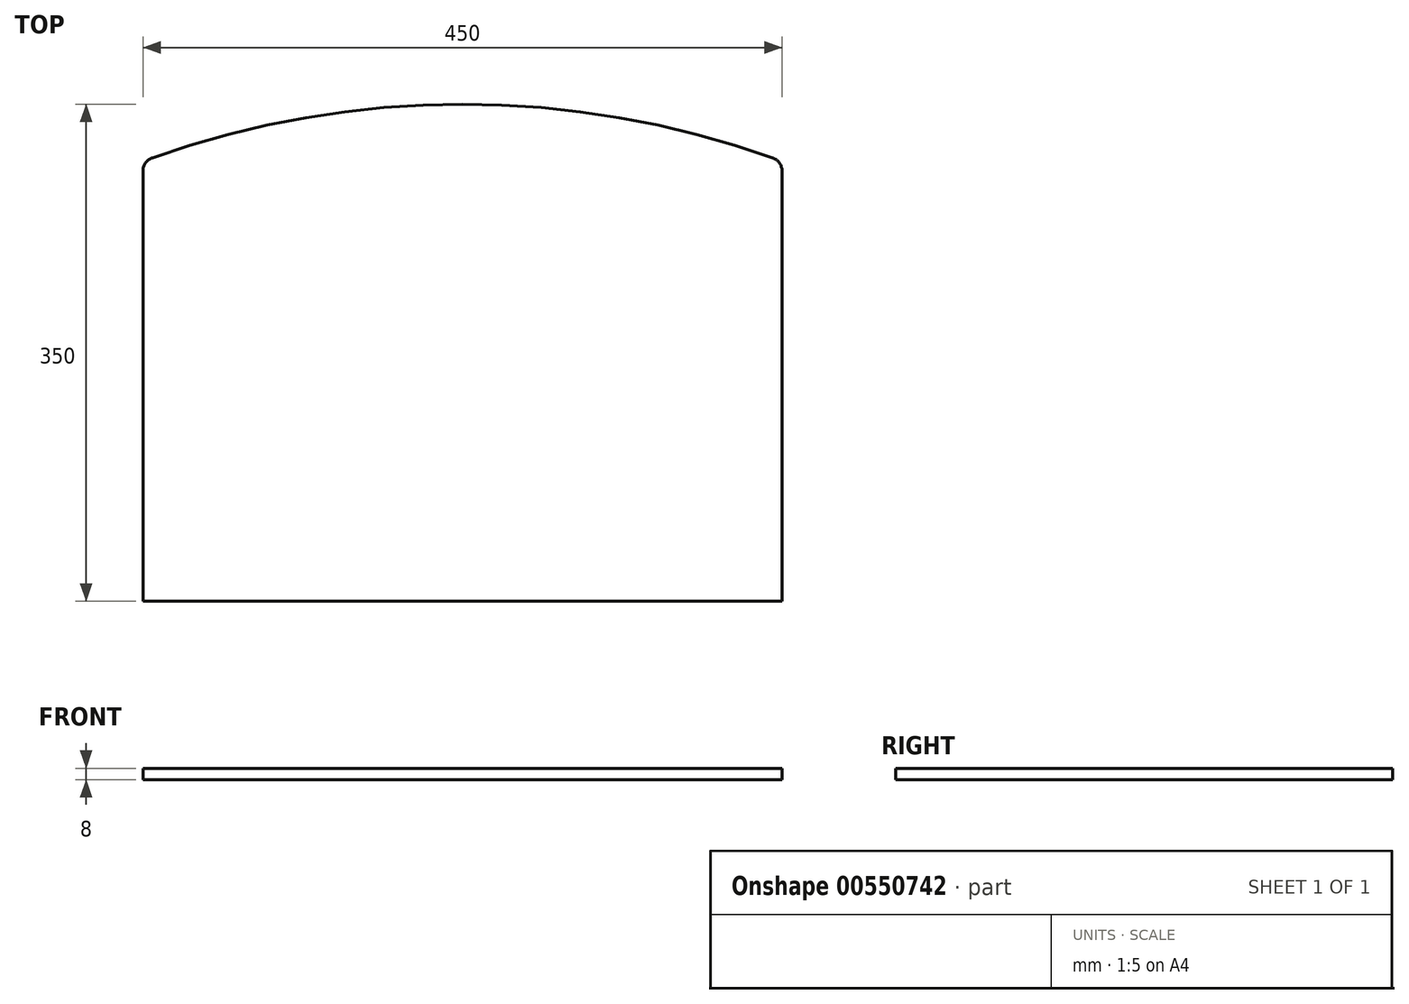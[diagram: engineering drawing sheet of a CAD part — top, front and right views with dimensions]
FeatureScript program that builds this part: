
annotation { "Feature Type Name" : "Feature", "Feature Type Description" : "" }
export const myFeature = defineFeature(function(context is Context, id is Id, definition is map)
    precondition{}
    {
        {
            var Q0;
            Q0=qCreatedBy(makeId("Top.planeOp"),FACE);
            var sketch = newSketch(context, id + "F0", { "sketchPlane" : qUnion([Q0])});
            skLineSegment(sketch, "E0", {"start": v(-175.59, -113.68) * mm, "end": v(274.41, -113.68) * mm});
            skLineSegment(sketch, "E1", {"start": v(-175.59, -113.68) * mm, "end": v(-175.59, 189.3) * mm});
            skLineSegment(sketch, "E2", {"start": v(274.41, -113.68) * mm, "end": v(274.41, 189.3) * mm});
            skArc(sketch, "E3", {"start": v(267.76, 198.72) * mm, "mid": v(49.41, 236.32) * mm, "end": v(-168.93, 198.72) * mm});
            skPoint(sketch, "E4.visualSharp", {"position": v(-175.59, 196.32) * mm});
            skArc(sketch, "E4.filletArc", {"start": v(-168.93, 198.72) * mm, "mid": v(-173.76, 195.07) * mm, "end": v(-175.59, 189.3) * mm});
            skPoint(sketch, "E5.visualSharp", {"position": v(274.41, 196.32) * mm});
            skArc(sketch, "E5.filletArc", {"start": v(274.41, 189.3) * mm, "mid": v(272.58, 195.07) * mm, "end": v(267.76, 198.72) * mm});
            skLineSegment(sketch, "E6", {"start": v(-120.82, 236.32) * mm, "end": v(-178.73, 236.32) * mm});
            skPoint(sketch, "E7.orphan", {"position": v(49.41, 236.32) * mm});
            skSolve(sketch);
        }
        {
            var Q0;
            Q0=makeQuery(id+"F0.imprint","IMPRINT",FACE,{"disambiguationData":[TD([[makeQuery(id+"F0.imprint","IMPRINT",EDGE,{"derivedFrom":sQuery(id+"F0.wireOp",EDGE,"E0")}),1.0]])]});
            extrude(context, id + "F1", {"entities" : qUnion([Q0]), "depth" : 8 * mm, "offsetDistance" : 25 * mm});
        }
    });
